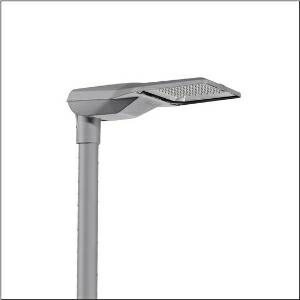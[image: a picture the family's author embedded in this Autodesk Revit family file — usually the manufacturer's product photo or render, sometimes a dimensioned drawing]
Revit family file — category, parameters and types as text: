
# Revit family: streetlight_sl_21_iq_midi___st0_5a_5xe3b41d08mb_eec4
name_source: partatom
category: Lighting Fixtures
units: mm (PartAtom-declared; Revit-internal decimal feet)

## family parameters
Cut with Voids When Loaded = No
Host = Face
Light Source = No
Part Type = Normal
Room Calculation Point = No
Round Connector Dimension = Use Diameter
Shared = No

## types (1)
- --- (1 x LED, 20360 lm, 146.7 W, 4000K)
    Apparent Load = 147 VA
    CIE Flux Codes = 41 75 97 100 100
    Color Rendering = 70
    Color Temperature = 4000K
    Default Elevation = 1800 mm
    Description = Streetlight SL 21 iQ midi, mast luminaire, primary light control with lens, of PMMA, primary optical cover: cover, of toughened safety glass, transparent, light distribution: ST0.5a, light emission: direct distribution, primary light characteristic: asymmetric, installation type: post-top, side-entry, LED, High Power LED, rated luminous flux: 20.360lm, luminous efficacy: 139lm/W, light colour: 740, colour temperature: 4000K, control gear: iQ-Comfort, control: Auto-Match, Temp-Guard, Lumen-Switch, Night-Set, Smart-Wire, Light-Fading, Desk-Remote (wireless, voltage-free reading and setting of iQ features in the workshop via application-optimized NFC function/RFID function), optimised constant luminous flux control (CLO 2.0), pre-setting: linear dimming characteristic, mains connection: 230..240V, AC, 50/60Hz, start of lifetime: 147W, end of service life: 161W, reduction: 62W, luminaire housing, of diecast aluminium, powder-coated, Siteco® metallic grey (DB 702S), corrosivity category C5 mid according to DIN EN ISO 12944, please order mast flange separately, inclination adjustable: 0°, 5°, 10°, 15°, sealing non-destructively replaceable, multi-level sealing system, length: 644mm, width: 335mm, height: 110mm, mast flange for spigot size: 42mm (side-entry): 5XC10008XM4, 60/48mm (side-entry/post-top): 5XC10108XM2, 76/60mm (side-entry/post-top): 5XC10108XM1, mounting height: 4..8m, protection rating (complete): IP66, insulation class (complete): insulation class II (safety insulation), certification: CE, ENEC, ENEC+, VDE, impact resistance: IK10, permissible operating ambient temperature for outdoor applications: -40..+50°C, standard-compliant lighting for roads and squares, packaging unit: 1 piece

Light Distribution: ST0.5a
    Height = 111 mm
    Lamp = 1 x LED
    Lamp Light Flux = 20360 lm
    Lamp Power = 146.7 W
    Lamp count = 1
    Length = 644 mm
    Luminous efficacy = 139 lm/W
    Manufacturer = Siteco
    ModVariant = No
    Model = 5XE3B41D08MB
    Number of Poles = 1
    OnlyDefault = Yes
    Power Factor = 1
    Product Name = Streetlight SL 21 iQ midi | ST0.5a
    Product group = mast luminaire | pylon top
    ProductGroupID = 6100
    Protection Class = Protection class II
    Protection Degree = IP 66
    RLX_Detail_Level = 1
    RLX_Emergency_Light_Flux = 0 lm
    RLX_Emergency_Type = 0
    RLX_Emergency_Type_DB = No
    RlxData = <blob elided: 37897 chars, md5=1a6fd90a>
    Socket = socket
    Standby Power = 0 W
    System Light Flux = 20360 lm
    System Power = 147 W
    Type Comments = factory setting: luminous flux: 100 % | dim-lin: 254 | 753 mA
    Type Image = l_1004298.jpg
    URL = http://relux.com
    VarID = @adj_191796
    Voltage = 0 V
    Weight = 0.00 kg
    Width = 336 mm

## geometry (parser evidence)
native form markers: Blend x4, Sweep x9
no freeform markers — native parametric forms only
